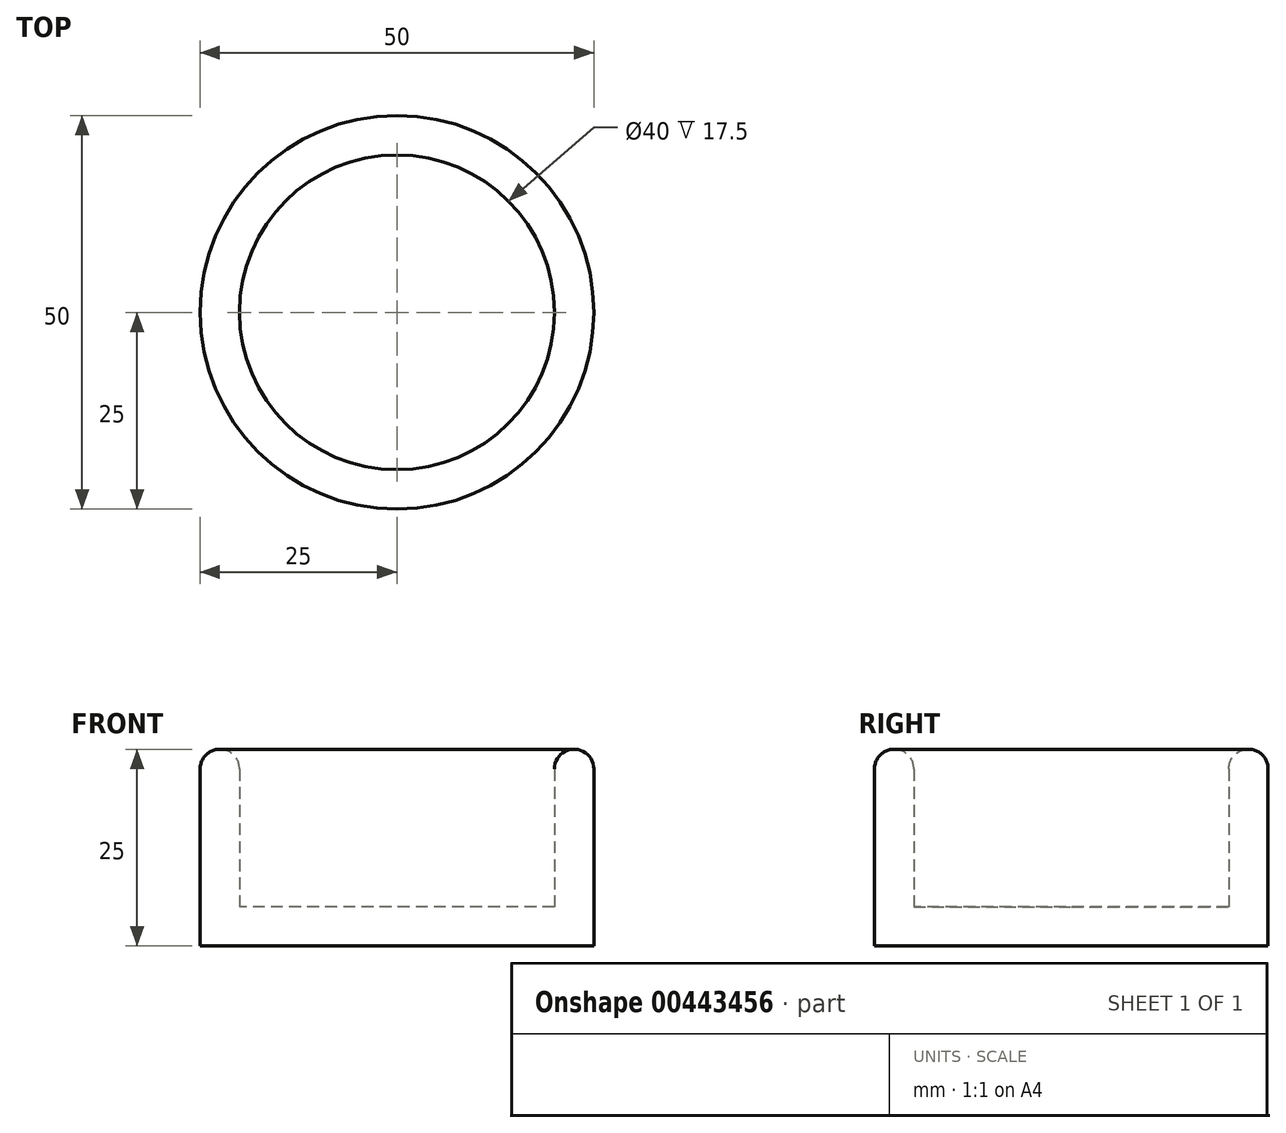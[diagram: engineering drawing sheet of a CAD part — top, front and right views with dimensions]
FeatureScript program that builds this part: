
annotation { "Feature Type Name" : "Feature", "Feature Type Description" : "" }
export const myFeature = defineFeature(function(context is Context, id is Id, definition is map)
    precondition{}
    {
        {
            var Q0;
            Q0=qCreatedBy(makeId("Top.planeOp"),FACE);
            var sketch = newSketch(context, id + "F0", { "sketchPlane" : qUnion([Q0])});
            skCircle(sketch, "E0", {"center": v(0, 0) * mm, "radius": 25 * mm});
            skCircle(sketch, "E1", {"center": v(0, 0) * mm, "radius": 20 * mm});
            skSolve(sketch);
        }
        {
            var Q0;
            Q0 = qSketchRegion(id + "F0", true);
            extrude(context, id + "F1", {"entities" : qUnion([Q0]), "depth" : 20 * mm});
        }
        {
            var Q0;
            Q0=makeQuery(id+"F1.opExtrude","CAP_FACE",FACE,{"disambiguationData":[OSD([sQuery(id+"F0.wireOp",EDGE,"E0"),sQuery(id+"F0.wireOp",EDGE,"E1")])],"isStart":true});
            var sketch = newSketch(context, id + "F2", { "sketchPlane" : qUnion([Q0])});
            skCircle(sketch, "E2", {"center": v(0, 0) * mm, "radius": 25 * mm});
            skSolve(sketch);
        }
        {
            var Q0;
            Q0 = qSketchRegion(id + "F2", true);
            extrude(context, id + "F3", {"entities" : qUnion([Q0]), "operationType" : NewBodyOperationType.ADD, "depth" : 5 * mm});
        }
        {
            var Q0;
            Q0=makeQuery(id+"F1.opExtrude","CAP_EDGE",EDGE,{"disambiguationData":[OSD([sQuery(id+"F0.wireOp",EDGE,"E0")])],"isStart":false});
            fillet(context, id + "F4", {"entities" : qUnion([Q0]), "radius" : 2.5 * mm, "tangentPropagation" : true, "allowEdgeOverflow" : false});
        }
        {
            var Q0;
            Q0=makeQuery(id+"F1.opExtrude","CAP_EDGE",EDGE,{"disambiguationData":[OSD([sQuery(id+"F0.wireOp",EDGE,"E1")])],"isStart":false});
            fillet(context, id + "F5", {"entities" : qUnion([Q0]), "radius" : 2.5 * mm, "tangentPropagation" : true, "allowEdgeOverflow" : false});
        }
    });
